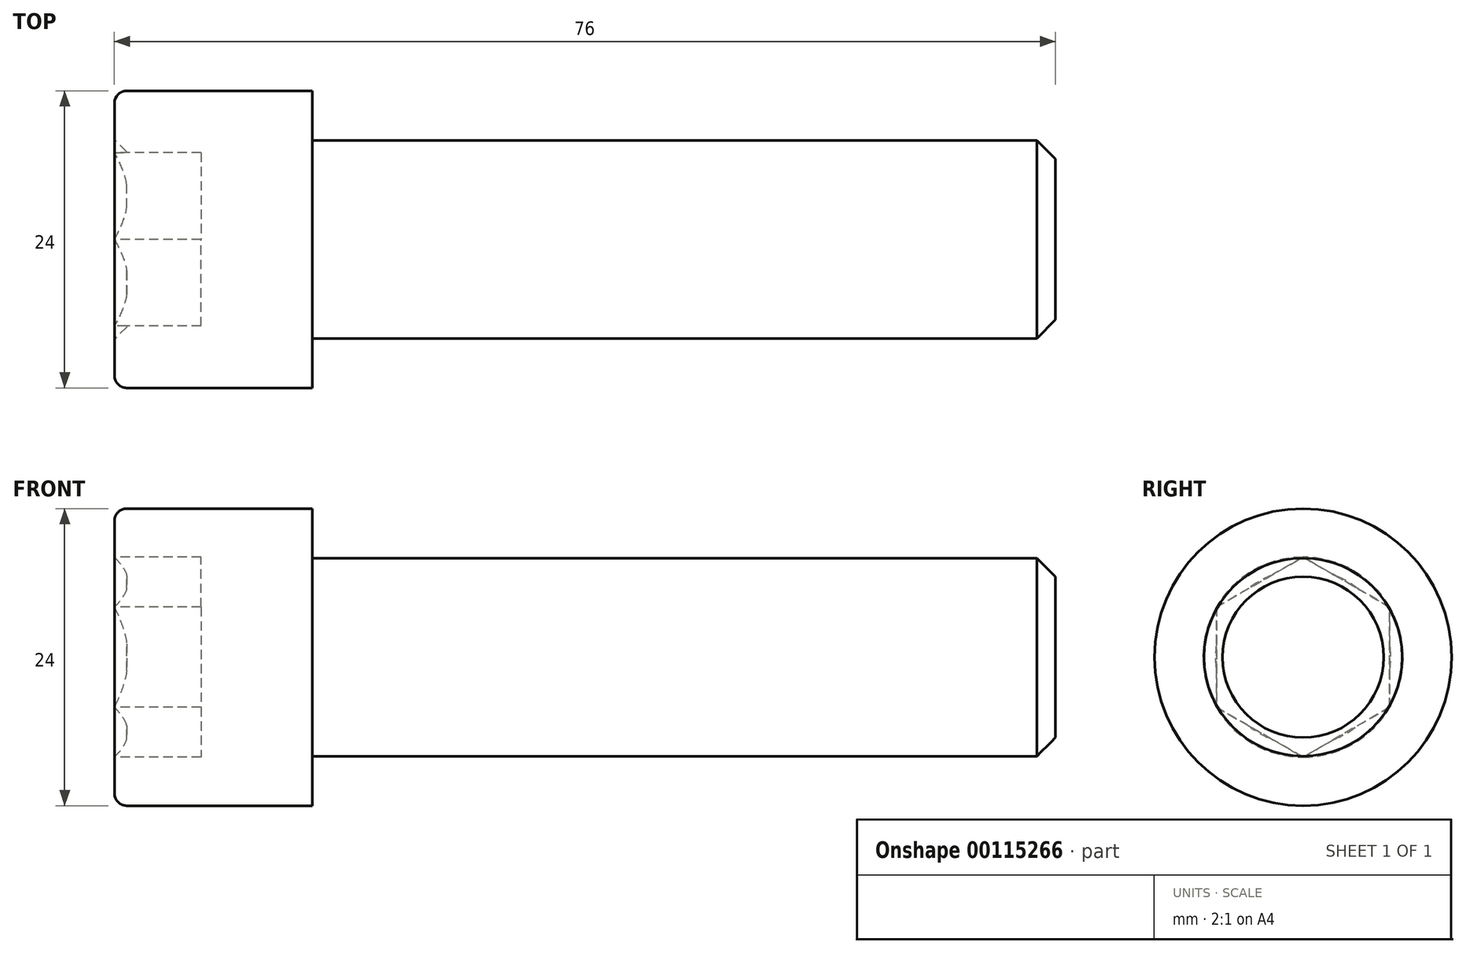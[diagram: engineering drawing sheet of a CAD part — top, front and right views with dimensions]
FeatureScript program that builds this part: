
annotation { "Feature Type Name" : "Feature", "Feature Type Description" : "" }
export const myFeature = defineFeature(function(context is Context, id is Id, definition is map)
    precondition{}
    {
        {
            var Q0;
            Q0=qCreatedBy(makeId("Top.planeOp"),FACE);
            var sketch = newSketch(context, id + "F0", { "sketchPlane" : qUnion([Q0])});
            skLineSegment(sketch, "E0", {"start": v(-38, 0) * mm, "end": v(39.08, 0) * mm, "construction": true});
            skLineSegment(sketch, "E1", {"start": v(-30.75, 0) * mm, "end": v(-30.75, 12) * mm});
            skLineSegment(sketch, "E2", {"start": v(-30.75, 12) * mm, "end": v(-14.75, 12) * mm});
            skLineSegment(sketch, "E3", {"start": v(-14.75, 12) * mm, "end": v(-14.75, 8) * mm});
            skLineSegment(sketch, "E4", {"start": v(-14.75, 8) * mm, "end": v(45.25, 8) * mm});
            skLineSegment(sketch, "E5", {"start": v(45.25, 8) * mm, "end": v(45.25, 0) * mm});
            skLineSegment(sketch, "E6", {"start": v(-30.75, 0) * mm, "end": v(45.25, 0) * mm});
            skSolve(sketch);
        }
        {
            var Q0;
            Q0=qSketchRegion(id+"F0",true);
            var Q1;
            Q1=sQuery(id+"F0.wireOp",EDGE,"E0");
            revolve(context, id + "F1", {"entities" : qUnion([Q0]), "axis" : qUnion([Q1]), "revolveType" : RevolveType.FULL});
        }
        {
            var Q0;
            Q0=makeQuery(id+"F1.opRevolve","SWEPT_EDGE",EDGE,{"disambiguationData":[OSD([sQuery(id+"F0.wireOp",EDGE,"E1"),sQuery(id+"F0.wireOp",EDGE,"E2")])]});
            fillet(context, id + "F2", {"entities" : qUnion([Q0]), "radius" : 1 * mm, "tangentPropagation" : true, "allowEdgeOverflow" : false});
        }
        {
            var Q0;
            Q0=makeQuery(id+"F1.opRevolve","SWEPT_EDGE",EDGE,{"disambiguationData":[OSD([sQuery(id+"F0.wireOp",EDGE,"E4"),sQuery(id+"F0.wireOp",EDGE,"E5")])]});
            chamfer(context, id + "F3", {"entities" : qUnion([Q0]), "width" : 1.5 * mm, "tangentPropagation" : true});
        }
        {
            var Q0;
            Q0=makeQuery(id+"F1.opRevolve","SWEPT_FACE",FACE,{"disambiguationData":[OSD([sQuery(id+"F0.wireOp",EDGE,"E1")])]});
            var sketch = newSketch(context, id + "F4", { "sketchPlane" : qUnion([Q0])});
            skPoint(sketch, "E7", {"position": v(0, 0) * mm});
            skLineSegment(sketch, "E8", {"start": v(0, 0) * mm, "end": v(0, 0) * mm});
            skLineSegment(sketch, "E9", {"start": v(7, 2.45) * mm, "end": v(7, 4.04) * mm});
            skLineSegment(sketch, "E10", {"start": v(7, 4.04) * mm, "end": v(0, 8.08) * mm});
            skLineSegment(sketch, "E11.MirrorCS", {"start": v(7, -4.04) * mm, "end": v(0, -8.08) * mm});
            skLineSegment(sketch, "E12.MirrorCS", {"start": v(7, 2.45) * mm, "end": v(7, -4.04) * mm});
            skLineSegment(sketch, "E13.MirrorCS", {"start": v(-7, -4.04) * mm, "end": v(0, -8.08) * mm});
            skLineSegment(sketch, "E14.MirrorCS", {"start": v(-7, 2.45) * mm, "end": v(-7, -4.04) * mm});
            skLineSegment(sketch, "E15.MirrorCS", {"start": v(-7, 2.45) * mm, "end": v(-7, 4.04) * mm});
            skLineSegment(sketch, "E16.MirrorCS", {"start": v(-7, 4.04) * mm, "end": v(0, 8.08) * mm});
            skLineSegment(sketch, "E17", {"start": v(4.27, 2.46) * mm, "end": v(-5.2, -3) * mm, "construction": true});
            skSolve(sketch);
        }
        {
            var Q0;
            Q0=makeQuery(id+"F4.imprint","IMPRINT",FACE,{"disambiguationData":[TD([[makeQuery(id+"F4.imprint","IMPRINT",EDGE,{"derivedFrom":sQuery(id+"F4.wireOp",EDGE,"E9")}),1.0]])]});
            extrude(context, id + "F5", {"entities" : qUnion([Q0]), "operationType" : NewBodyOperationType.REMOVE, "oppositeDirection" : true, "depth" : 7 * mm});
        }
        {
            var Q0;
            Q0=qCreatedBy(makeId("Front.planeOp"),FACE);
            var sketch = newSketch(context, id + "F6", { "sketchPlane" : qUnion([Q0])});
            skLineSegment(sketch, "E18", {"start": v(-30.75, 8.08) * mm, "end": v(-29.75, 7.08) * mm});
            skLineSegment(sketch, "E19", {"start": v(-29.75, 7.08) * mm, "end": v(-29.75, 0) * mm});
            skLineSegment(sketch, "E20", {"start": v(-29.75, 0) * mm, "end": v(-30.75, 0) * mm});
            skLineSegment(sketch, "E21", {"start": v(-30.75, 0) * mm, "end": v(-30.75, 8.08) * mm});
            skSolve(sketch);
        }
        {
            var Q0;
            Q0=qSketchRegion(id+"F6",true);
            var Q1;
            Q1=sQuery(id+"F0.wireOp",EDGE,"E0");
            revolve(context, id + "F7", {"operationType" : NewBodyOperationType.REMOVE, "entities" : qUnion([Q0]), "axis" : qUnion([Q1]), "revolveType" : RevolveType.FULL, "oppositeDirection" : true});
        }
        {
            var Q0;
            Q0=makeQuery(id+"F1.opRevolve","SWEPT_BODY",BODY,{"disambiguationData":[OSD([sQuery(id+"F0.wireOp",EDGE,"E1"),sQuery(id+"F0.wireOp",EDGE,"E2"),sQuery(id+"F0.wireOp",EDGE,"E3"),sQuery(id+"F0.wireOp",EDGE,"E4"),sQuery(id+"F0.wireOp",EDGE,"E5"),sQuery(id+"F0.wireOp",EDGE,"E6")])]});
            transform(context, id + "F8", {"entities" : qUnion([Q0]), "transformType" : TransformType.TRANSLATION_3D, "dx" : 0 * mm, "dy" : 0 * mm, "dz" : 0 * mm, "makeCopy" : true});
        }
        {
            var Q0;
            Q0=makeQuery(id+"F8.opPattern","COPY",BODY,{"derivedFrom":makeQuery(id+"F1.opRevolve","SWEPT_BODY",BODY,{"disambiguationData":[OSD([sQuery(id+"F0.wireOp",EDGE,"E1"),sQuery(id+"F0.wireOp",EDGE,"E2"),sQuery(id+"F0.wireOp",EDGE,"E3"),sQuery(id+"F0.wireOp",EDGE,"E4"),sQuery(id+"F0.wireOp",EDGE,"E5"),sQuery(id+"F0.wireOp",EDGE,"E6")])]}),"instanceName":"1"});
            deleteBodies(context, id + "F9", {"entities" : qUnion([Q0])});
        }
    });
